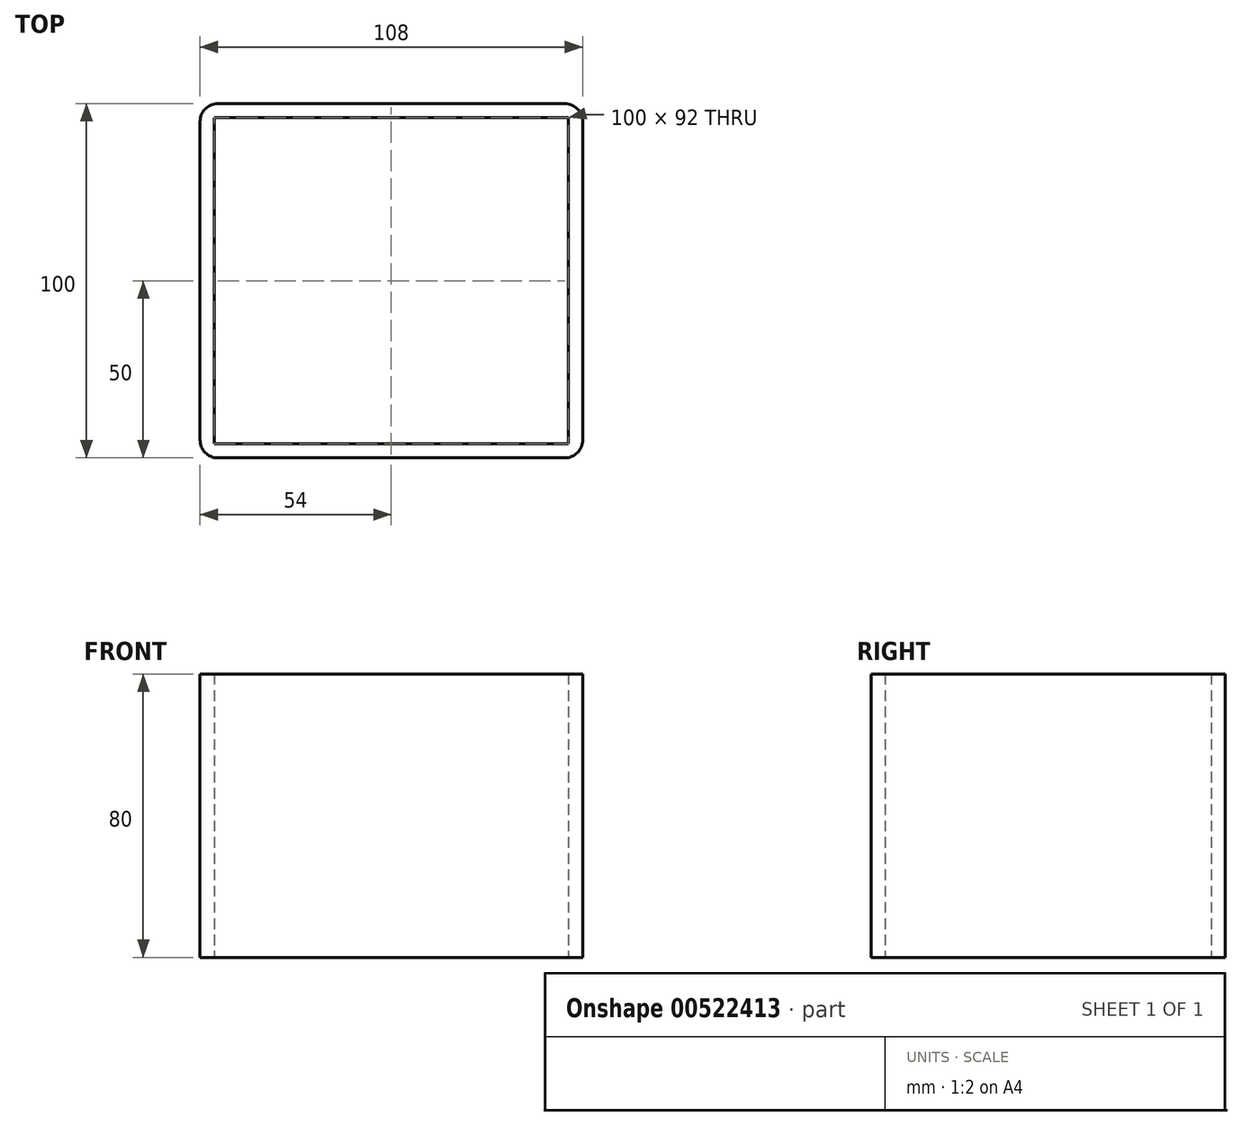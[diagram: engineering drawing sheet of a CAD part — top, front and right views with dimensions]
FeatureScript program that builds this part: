
annotation { "Feature Type Name" : "Feature", "Feature Type Description" : "" }
export const myFeature = defineFeature(function(context is Context, id is Id, definition is map)
    precondition{}
    {
        {
            var Q0;
            Q0=qCreatedBy(makeId("Top.planeOp"),FACE);
            var sketch = newSketch(context, id + "F0", { "sketchPlane" : qUnion([Q0])});
            skLineSegment(sketch, "E0.bottom", {"start": v(54, 50) * mm, "end": v(-54, 50) * mm});
            skLineSegment(sketch, "E0.top", {"start": v(54, -50) * mm, "end": v(-54, -50) * mm});
            skLineSegment(sketch, "E0.left", {"start": v(54, 50) * mm, "end": v(54, -50) * mm});
            skLineSegment(sketch, "E0.right", {"start": v(-54, 50) * mm, "end": v(-54, -50) * mm});
            skPoint(sketch, "E0.middle", {"position": v(0, 0) * mm});
            skLineSegment(sketch, "E1.0", {"start": v(-50, 46) * mm, "end": v(-50, -46) * mm});
            skLineSegment(sketch, "E1.1", {"start": v(50, 46) * mm, "end": v(-50, 46) * mm});
            skLineSegment(sketch, "E1.2", {"start": v(50, 46) * mm, "end": v(50, -46) * mm});
            skLineSegment(sketch, "E1.3", {"start": v(50, -46) * mm, "end": v(-50, -46) * mm});
            skSolve(sketch);
        }
        {
            var Q0;
            Q0 = qSketchRegion(id + "F0", true);
            extrude(context, id + "F1", {"entities" : qUnion([Q0]), "depth" : 80 * mm, "offsetDistance" : 25.4 * mm});
        }
        {
            var Q0;
            Q0=makeQuery(id+"F1.opExtrude","SWEPT_EDGE",EDGE,{"disambiguationData":[OSD([sQuery(id+"F0.wireOp",EDGE,"E0.top"),sQuery(id+"F0.wireOp",EDGE,"E0.right")])]});
            fillet(context, id + "F2", {"entities" : qUnion([Q0]), "radius" : 5.08 * mm, "tangentPropagation" : true, "allowEdgeOverflow" : false});
        }
        {
            var Q0;
            Q0=makeQuery(id+"F1.opExtrude","SWEPT_EDGE",EDGE,{"disambiguationData":[OSD([sQuery(id+"F0.wireOp",EDGE,"E0.top"),sQuery(id+"F0.wireOp",EDGE,"E0.left")])]});
            var Q1;
            Q1=makeQuery(id+"F1.opExtrude","SWEPT_EDGE",EDGE,{"disambiguationData":[OSD([sQuery(id+"F0.wireOp",EDGE,"E0.bottom"),sQuery(id+"F0.wireOp",EDGE,"E0.left")])]});
            var Q2;
            Q2=makeQuery(id+"F1.opExtrude","SWEPT_EDGE",EDGE,{"disambiguationData":[OSD([sQuery(id+"F0.wireOp",EDGE,"E0.bottom"),sQuery(id+"F0.wireOp",EDGE,"E0.right")])]});
            fillet(context, id + "F3", {"entities" : qUnion([Q0, Q1, Q2]), "radius" : 5.08 * mm, "tangentPropagation" : true, "allowEdgeOverflow" : false});
        }
    });
